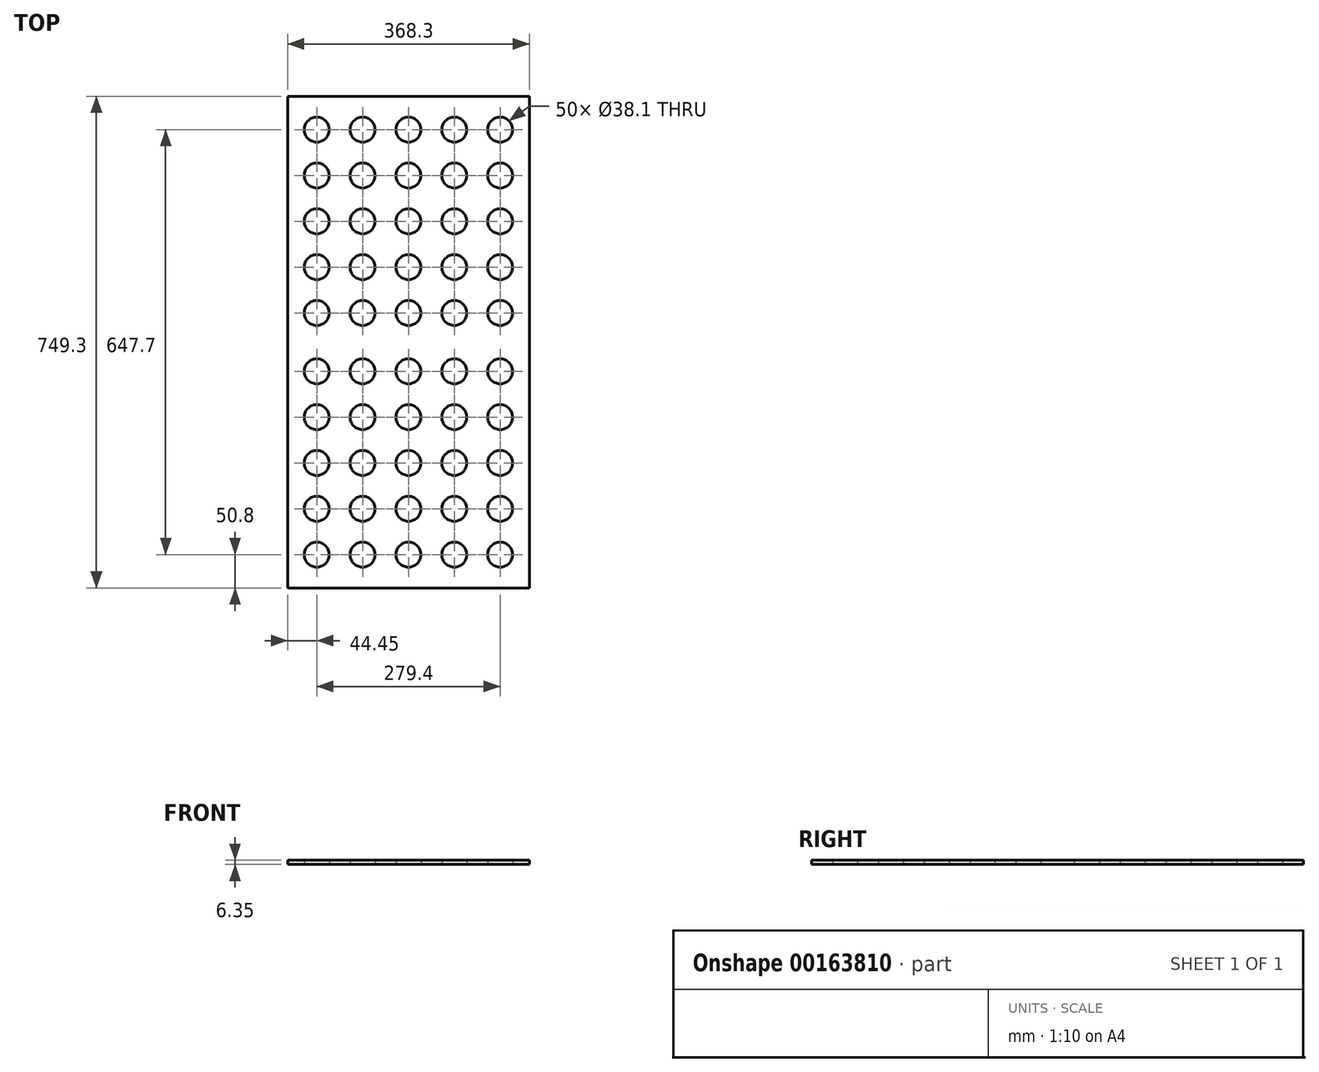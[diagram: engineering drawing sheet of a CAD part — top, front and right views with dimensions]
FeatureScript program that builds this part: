
annotation { "Feature Type Name" : "Feature", "Feature Type Description" : "" }
export const myFeature = defineFeature(function(context is Context, id is Id, definition is map)
    precondition{}
    {
        {
            var Q0;
            Q0=qCreatedBy(makeId("Top.planeOp"),FACE);
            var sketch = newSketch(context, id + "F0", { "sketchPlane" : qUnion([Q0])});
            skLineSegment(sketch, "E0.bottom", {"start": v(184.15, 374.65) * mm, "end": v(-184.15, 374.65) * mm});
            skLineSegment(sketch, "E0.top", {"start": v(184.15, -374.65) * mm, "end": v(-184.15, -374.65) * mm});
            skLineSegment(sketch, "E0.left", {"start": v(184.15, 374.65) * mm, "end": v(184.15, -374.65) * mm});
            skLineSegment(sketch, "E0.right", {"start": v(-184.15, 374.65) * mm, "end": v(-184.15, -374.65) * mm});
            skPoint(sketch, "E0.middle", {"position": v(0, 0) * mm});
            skCircle(sketch, "E1", {"center": v(-139.7, -323.85) * mm, "radius": 19.05 * mm});
            skCircle(sketch, "E2.0.1.0", {"center": v(-139.7, -254) * mm, "radius": 19.05 * mm});
            skCircle(sketch, "E2.0.2.0", {"center": v(-139.7, -184.15) * mm, "radius": 19.05 * mm});
            skCircle(sketch, "E2.0.3.0", {"center": v(-139.7, -114.3) * mm, "radius": 19.05 * mm});
            skCircle(sketch, "E2.0.4.0", {"center": v(-139.7, -44.45) * mm, "radius": 19.05 * mm});
            skCircle(sketch, "E2.1.0.0", {"center": v(-69.85, -323.85) * mm, "radius": 19.05 * mm});
            skCircle(sketch, "E2.1.1.0", {"center": v(-69.85, -254) * mm, "radius": 19.05 * mm});
            skCircle(sketch, "E2.1.2.0", {"center": v(-69.85, -184.15) * mm, "radius": 19.05 * mm});
            skCircle(sketch, "E2.1.3.0", {"center": v(-69.85, -114.3) * mm, "radius": 19.05 * mm});
            skCircle(sketch, "E2.1.4.0", {"center": v(-69.85, -44.45) * mm, "radius": 19.05 * mm});
            skCircle(sketch, "E2.2.0.0", {"center": v(0, -323.85) * mm, "radius": 19.05 * mm});
            skCircle(sketch, "E2.2.1.0", {"center": v(0, -254) * mm, "radius": 19.05 * mm});
            skCircle(sketch, "E2.2.2.0", {"center": v(0, -184.15) * mm, "radius": 19.05 * mm});
            skCircle(sketch, "E2.2.3.0", {"center": v(0, -114.3) * mm, "radius": 19.05 * mm});
            skCircle(sketch, "E2.2.4.0", {"center": v(0, -44.45) * mm, "radius": 19.05 * mm});
            skCircle(sketch, "E2.3.0.0", {"center": v(69.85, -323.85) * mm, "radius": 19.05 * mm});
            skCircle(sketch, "E2.3.1.0", {"center": v(69.85, -254) * mm, "radius": 19.05 * mm});
            skCircle(sketch, "E2.3.2.0", {"center": v(69.85, -184.15) * mm, "radius": 19.05 * mm});
            skCircle(sketch, "E2.3.3.0", {"center": v(69.85, -114.3) * mm, "radius": 19.05 * mm});
            skCircle(sketch, "E2.3.4.0", {"center": v(69.85, -44.45) * mm, "radius": 19.05 * mm});
            skCircle(sketch, "E2.4.0.0", {"center": v(139.7, -323.85) * mm, "radius": 19.05 * mm});
            skCircle(sketch, "E2.4.1.0", {"center": v(139.7, -254) * mm, "radius": 19.05 * mm});
            skCircle(sketch, "E2.4.2.0", {"center": v(139.7, -184.15) * mm, "radius": 19.05 * mm});
            skCircle(sketch, "E2.4.3.0", {"center": v(139.7, -114.3) * mm, "radius": 19.05 * mm});
            skCircle(sketch, "E2.4.4.0", {"center": v(139.7, -44.45) * mm, "radius": 19.05 * mm});
            skLineSegment(sketch, "E2.direction1", {"start": v(-139.7, -323.85) * mm, "end": v(-69.85, -323.85) * mm, "construction": true});
            skLineSegment(sketch, "E3", {"start": v(-184.15, 0) * mm, "end": v(184.15, 0) * mm, "construction": true});
            skCircle(sketch, "E4.MirrorC", {"center": v(-139.7, 323.85) * mm, "radius": 19.05 * mm});
            skCircle(sketch, "E5.MirrorC", {"center": v(-69.85, 323.85) * mm, "radius": 19.05 * mm});
            skCircle(sketch, "E6.MirrorC", {"center": v(0, 323.85) * mm, "radius": 19.05 * mm});
            skCircle(sketch, "E7.MirrorC", {"center": v(69.85, 323.85) * mm, "radius": 19.05 * mm});
            skCircle(sketch, "E8.MirrorC", {"center": v(139.7, 323.85) * mm, "radius": 19.05 * mm});
            skCircle(sketch, "E9.MirrorC", {"center": v(139.7, 254) * mm, "radius": 19.05 * mm});
            skCircle(sketch, "E10.MirrorC", {"center": v(69.85, 254) * mm, "radius": 19.05 * mm});
            skCircle(sketch, "E11.MirrorC", {"center": v(0, 254) * mm, "radius": 19.05 * mm});
            skCircle(sketch, "E12.MirrorC", {"center": v(-69.85, 254) * mm, "radius": 19.05 * mm});
            skCircle(sketch, "E13.MirrorC", {"center": v(-139.7, 254) * mm, "radius": 19.05 * mm});
            skCircle(sketch, "E14.MirrorC", {"center": v(-139.7, 184.15) * mm, "radius": 19.05 * mm});
            skCircle(sketch, "E15.MirrorC", {"center": v(-69.85, 184.15) * mm, "radius": 19.05 * mm});
            skCircle(sketch, "E16.MirrorC", {"center": v(0, 184.15) * mm, "radius": 19.05 * mm});
            skCircle(sketch, "E17.MirrorC", {"center": v(69.85, 184.15) * mm, "radius": 19.05 * mm});
            skCircle(sketch, "E18.MirrorC", {"center": v(139.7, 184.15) * mm, "radius": 19.05 * mm});
            skCircle(sketch, "E19.MirrorC", {"center": v(139.7, 114.3) * mm, "radius": 19.05 * mm});
            skCircle(sketch, "E20.MirrorC", {"center": v(69.85, 114.3) * mm, "radius": 19.05 * mm});
            skCircle(sketch, "E21.MirrorC", {"center": v(0, 114.3) * mm, "radius": 19.05 * mm});
            skCircle(sketch, "E22.MirrorC", {"center": v(-69.85, 114.3) * mm, "radius": 19.05 * mm});
            skCircle(sketch, "E23.MirrorC", {"center": v(-139.7, 114.3) * mm, "radius": 19.05 * mm});
            skCircle(sketch, "E24.MirrorC", {"center": v(-139.7, 44.45) * mm, "radius": 19.05 * mm});
            skCircle(sketch, "E25.MirrorC", {"center": v(-69.85, 44.45) * mm, "radius": 19.05 * mm});
            skCircle(sketch, "E26.MirrorC", {"center": v(0, 44.45) * mm, "radius": 19.05 * mm});
            skCircle(sketch, "E27.MirrorC", {"center": v(69.85, 44.45) * mm, "radius": 19.05 * mm});
            skCircle(sketch, "E28.MirrorC", {"center": v(139.7, 44.45) * mm, "radius": 19.05 * mm});
            skSolve(sketch);
        }
        {
            var Q0;
            Q0=makeQuery(id+"F0.imprint","IMPRINT",FACE,{"disambiguationData":[TD([[makeQuery(id+"F0.imprint","IMPRINT",EDGE,{"derivedFrom":sQuery(id+"F0.wireOp",EDGE,"E0.bottom")}),1.0]])]});
            extrude(context, id + "F1", {"entities" : qUnion([Q0]), "depth" : 6.35 * mm});
        }
    });
